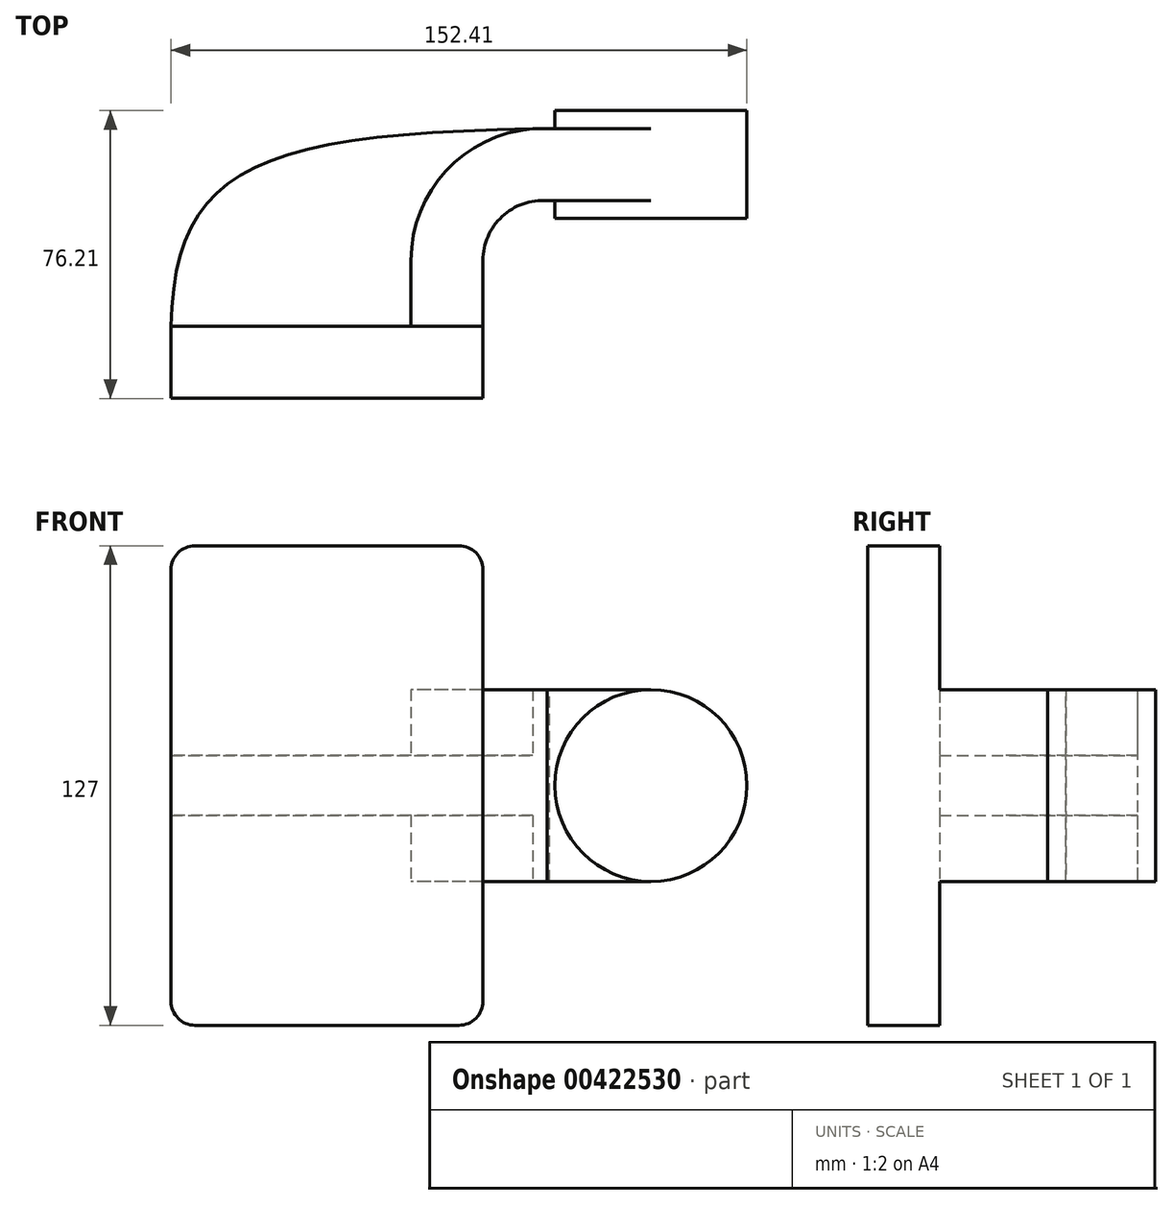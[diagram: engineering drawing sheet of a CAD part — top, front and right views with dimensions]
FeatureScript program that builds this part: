
annotation { "Feature Type Name" : "Feature", "Feature Type Description" : "" }
export const myFeature = defineFeature(function(context is Context, id is Id, definition is map)
    precondition{}
    {
        {
            var Q0;
            Q0=qCreatedBy(makeId("Top.planeOp"),FACE);
            var sketch = newSketch(context, id + "F0", { "sketchPlane" : qUnion([Q0])});
            skLineSegment(sketch, "E0.bottom", {"start": v(41.27, 9.53) * mm, "end": v(-41.28, 9.53) * mm});
            skLineSegment(sketch, "E0.top", {"start": v(41.28, -9.52) * mm, "end": v(-41.27, -9.52) * mm});
            skLineSegment(sketch, "E0.left", {"start": v(41.28, 9.53) * mm, "end": v(41.28, -9.52) * mm});
            skLineSegment(sketch, "E0.right", {"start": v(-41.28, 9.53) * mm, "end": v(-41.27, -9.52) * mm});
            skPoint(sketch, "E0.middle", {"position": v(0, 0) * mm});
            skLineSegment(sketch, "E1.bottom", {"start": v(60.32, 38.1) * mm, "end": v(111.12, 38.1) * mm});
            skLineSegment(sketch, "E1.top", {"start": v(60.32, 66.68) * mm, "end": v(111.12, 66.68) * mm});
            skLineSegment(sketch, "E1.left", {"start": v(60.32, 38.1) * mm, "end": v(60.32, 66.68) * mm});
            skLineSegment(sketch, "E1.right", {"start": v(111.13, 38.1) * mm, "end": v(111.12, 66.68) * mm});
            skPoint(sketch, "E1.middle", {"position": v(85.72, 52.39) * mm});
            skLineSegment(sketch, "E2", {"start": v(41.27, 9.53) * mm, "end": v(41.27, 27.03) * mm});
            skArc(sketch, "E3", {"start": v(41.27, 27.03) * mm, "mid": v(46.35, 38.66) * mm, "end": v(58.32, 42.86) * mm});
            skLineSegment(sketch, "E4", {"start": v(58.32, 42.86) * mm, "end": v(85.72, 42.86) * mm});
            skLineSegment(sketch, "E5.0", {"start": v(58.9, 61.91) * mm, "end": v(85.72, 61.91) * mm});
            skArc(sketch, "E5.1", {"start": v(22.22, 27.03) * mm, "mid": v(33.08, 52.34) * mm, "end": v(58.9, 61.91) * mm});
            skLineSegment(sketch, "E5.2", {"start": v(22.22, 9.53) * mm, "end": v(22.22, 27.03) * mm});
            skLineSegment(sketch, "E6", {"start": v(85.72, 38.1) * mm, "end": v(85.72, 66.68) * mm});
            skFitSpline(sketch, "E7", {"points": [v(-41.28, 9.53) * mm, v(58.9, 61.91) * mm], "startDerivative": vector(2.87, 125.47) * mm, "endDerivative": vector(234.91, 2.57) * mm});
            skSolve(sketch);
        }
        {
            var Q0;
            Q0=makeQuery(id+"F0.imprint","IMPRINT",FACE,{"disambiguationData":[TD([[makeQuery(id+"F0.imprint","IMPRINT",EDGE,{"derivedFrom":sQuery(id+"F0.wireOp",EDGE,"E0.top")}),-1.0]])]});
            extrude(context, id + "F1", {"entities" : qUnion([Q0]), "endBound" : BoundingType.SYMMETRIC, "depth" : 127 * mm});
        }
        {
            var Q0;
            {var subQ1=sQuery(id+"F0.wireOp",EDGE,"E2");Q0=makeQuery(id+"F0.imprint","IMPRINT",FACE,{"disambiguationData":[TD([[makeQuery(id+"F0.imprint","IMPRINT",EDGE,{"derivedFrom":subQ1}),1.0]])]});}
            var Q1;
            {var subQ0=sQuery(id+"F0.wireOp",EDGE,"E4");var subQ1=sQuery(id+"F0.wireOp",EDGE,"E1.left");var subQ2=makeQuery(id+"F0.imprint","INTERSECT",VERTEX,{"derivedFrom":[subQ1,subQ0]});Q1=makeQuery(id+"F0.imprint","IMPRINT",FACE,{"disambiguationData":[TD([[makeQuery(id+"F0.imprint","IMPRINT",EDGE,{"disambiguationData":[TD([[subQ2,-1.0]])],"derivedFrom":subQ1}),-1.0]])]});}
            extrude(context, id + "F2", {"entities" : qUnion([Q0, Q1]), "operationType" : NewBodyOperationType.ADD, "endBound" : BoundingType.SYMMETRIC, "depth" : 50.8 * mm});
        }
        {
            var Q0;
            {var subQ3=sQuery(id+"F0.wireOp",EDGE,"E5.2");Q0=makeQuery(id+"F0.imprint","IMPRINT",FACE,{"disambiguationData":[TD([[makeQuery(id+"F0.imprint","IMPRINT",EDGE,{"derivedFrom":subQ3}),1.0]])]});}
            extrude(context, id + "F3", {"entities" : qUnion([Q0]), "operationType" : NewBodyOperationType.ADD, "endBound" : BoundingType.SYMMETRIC, "depth" : 15.88 * mm});
        }
        {
            var Q0;
            {var subQ4=sQuery(id+"F0.wireOp",EDGE,"E1.right");Q0=makeQuery(id+"F0.imprint","IMPRINT",FACE,{"disambiguationData":[TD([[makeQuery(id+"F0.imprint","IMPRINT",EDGE,{"derivedFrom":subQ4}),1.0]])]});}
            var Q1;
            Q1=sQuery(id+"F0.wireOp",EDGE,"E6");
            revolve(context, id + "F4", {"operationType" : NewBodyOperationType.ADD, "entities" : qUnion([Q0]), "axis" : qUnion([Q1]), "revolveType" : RevolveType.FULL});
        }
        {
            var Q0;
            Q0=makeQuery(id+"F1.opExtrude","CAP_EDGE",EDGE,{"disambiguationData":[OSD([sQuery(id+"F0.wireOp",EDGE,"E0.right")])],"isStart":false});
            var Q1;
            Q1=makeQuery(id+"F1.opExtrude","CAP_EDGE",EDGE,{"disambiguationData":[OSD([sQuery(id+"F0.wireOp",EDGE,"E0.left")])],"isStart":false});
            var Q2;
            Q2=makeQuery(id+"F1.opExtrude","CAP_EDGE",EDGE,{"disambiguationData":[OSD([sQuery(id+"F0.wireOp",EDGE,"E0.left")])],"isStart":true});
            var Q3;
            Q3=makeQuery(id+"F1.opExtrude","CAP_EDGE",EDGE,{"disambiguationData":[OSD([sQuery(id+"F0.wireOp",EDGE,"E0.right")])],"isStart":true});
            fillet(context, id + "F5", {"entities" : qUnion([Q0, Q1, Q2, Q3]), "radius" : 6.35 * mm, "tangentPropagation" : true, "allowEdgeOverflow" : false});
        }
    });
